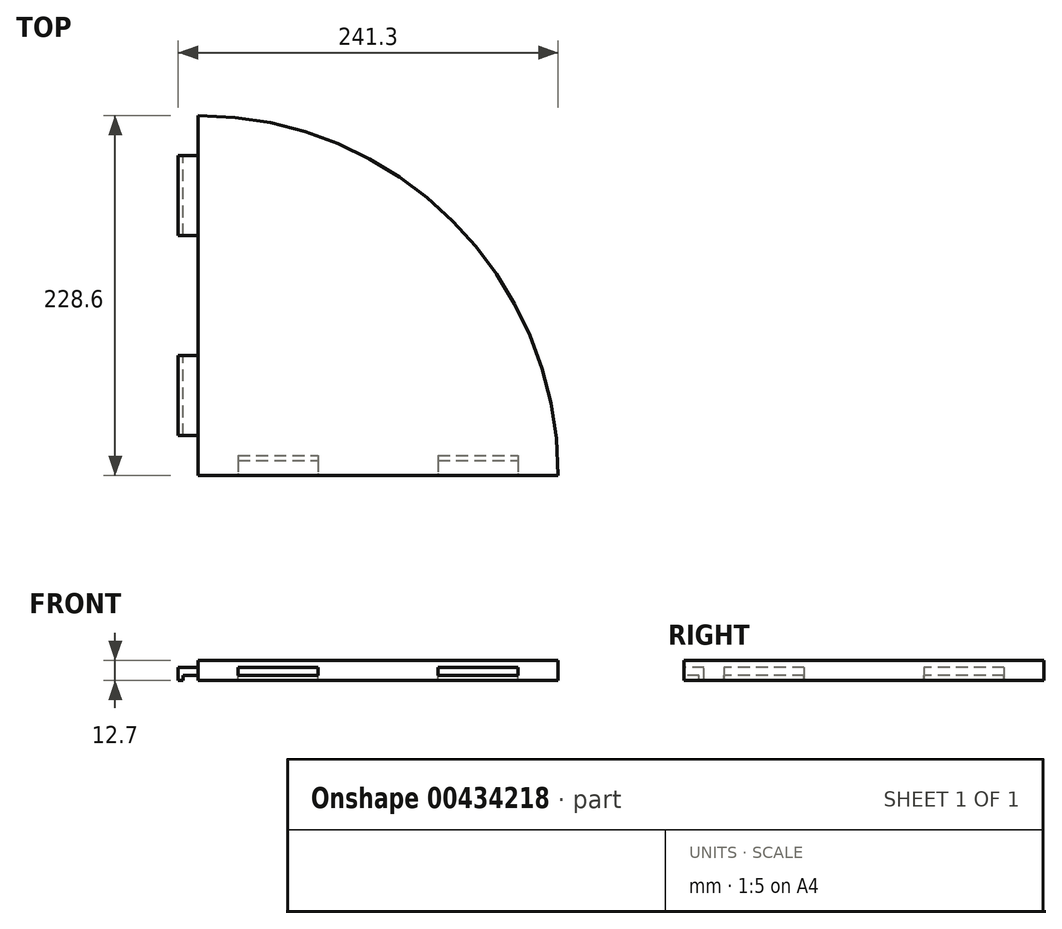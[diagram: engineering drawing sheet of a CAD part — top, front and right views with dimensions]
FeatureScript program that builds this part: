
annotation { "Feature Type Name" : "Feature", "Feature Type Description" : "" }
export const myFeature = defineFeature(function(context is Context, id is Id, definition is map)
    precondition{}
    {
        {
            var Q0;
            Q0=qCreatedBy(makeId("Top.planeOp"),FACE);
            var sketch = newSketch(context, id + "F0", { "sketchPlane" : qUnion([Q0])});
            skLineSegment(sketch, "E0", {"start": v(0, 0) * mm, "end": v(0, 228.6) * mm});
            skLineSegment(sketch, "E1", {"start": v(0, 0) * mm, "end": v(228.6, 0) * mm});
            skArc(sketch, "E2", {"start": v(0, 228.6) * mm, "mid": v(161.64, 161.64) * mm, "end": v(228.6, 0) * mm});
            skSolve(sketch);
        }
        {
            var Q0;
            Q0 = qSketchRegion(id + "F0", true);
            extrude(context, id + "F1", {"entities" : qUnion([Q0]), "depth" : 12.7 * mm});
        }
        {
            var Q0;
            Q0=makeQuery(id+"F1.opExtrude","SWEPT_FACE",FACE,{"disambiguationData":[OSD([sQuery(id+"F0.wireOp",EDGE,"E1")])]});
            var sketch = newSketch(context, id + "F2", { "sketchPlane" : qUnion([Q0])});
            skLineSegment(sketch, "E3.bottom", {"start": v(25.4, 3.18) * mm, "end": v(76.2, 3.18) * mm});
            skLineSegment(sketch, "E3.top", {"start": v(25.4, 8.26) * mm, "end": v(76.2, 8.26) * mm});
            skLineSegment(sketch, "E3.left", {"start": v(25.4, 3.18) * mm, "end": v(25.4, 8.26) * mm});
            skLineSegment(sketch, "E3.right", {"start": v(76.2, 3.18) * mm, "end": v(76.2, 8.25) * mm});
            skLineSegment(sketch, "E4.bottom", {"start": v(152.4, 3.18) * mm, "end": v(203.2, 3.18) * mm});
            skLineSegment(sketch, "E4.top", {"start": v(152.4, 8.25) * mm, "end": v(203.2, 8.25) * mm});
            skLineSegment(sketch, "E4.left", {"start": v(152.4, 3.18) * mm, "end": v(152.4, 8.25) * mm});
            skLineSegment(sketch, "E4.right", {"start": v(203.2, 3.18) * mm, "end": v(203.2, 8.26) * mm});
            skSolve(sketch);
        }
        {
            var Q0;
            Q0 = qSketchRegion(id + "F2", true);
            extrude(context, id + "F3", {"entities" : qUnion([Q0]), "operationType" : NewBodyOperationType.REMOVE, "oppositeDirection" : true, "depth" : 12.7 * mm, "offsetDistance" : 25.4 * mm});
        }
        {
            var Q0;
            Q0=makeQuery(id+"F1.opExtrude","SWEPT_FACE",FACE,{"disambiguationData":[OSD([sQuery(id+"F0.wireOp",EDGE,"E0")])]});
            var sketch = newSketch(context, id + "F4", { "sketchPlane" : qUnion([Q0])});
            skLineSegment(sketch, "E5.bottom", {"start": v(-76.2, 8.26) * mm, "end": v(-25.4, 8.26) * mm});
            skLineSegment(sketch, "E5.top", {"start": v(-76.2, 3.17) * mm, "end": v(-25.4, 3.17) * mm});
            skLineSegment(sketch, "E5.left", {"start": v(-76.2, 8.26) * mm, "end": v(-76.2, 3.17) * mm});
            skLineSegment(sketch, "E5.right", {"start": v(-25.4, 8.26) * mm, "end": v(-25.4, 3.18) * mm});
            skLineSegment(sketch, "E6.bottom", {"start": v(-203.2, 8.26) * mm, "end": v(-152.4, 8.26) * mm});
            skLineSegment(sketch, "E6.top", {"start": v(-203.2, 3.17) * mm, "end": v(-152.4, 3.17) * mm});
            skLineSegment(sketch, "E6.left", {"start": v(-203.2, 8.26) * mm, "end": v(-203.2, 3.18) * mm});
            skLineSegment(sketch, "E6.right", {"start": v(-152.4, 8.26) * mm, "end": v(-152.4, 3.18) * mm});
            skSolve(sketch);
        }
        {
            var Q0;
            Q0 = qSketchRegion(id + "F4", true);
            extrude(context, id + "F5", {"entities" : qUnion([Q0]), "operationType" : NewBodyOperationType.ADD, "depth" : 12.7 * mm, "offsetDistance" : 25.4 * mm});
        }
        {
            var Q0;
            Q0=makeQuery(id+"F3.boolean.opBoolean","COPY",FACE,{"derivedFrom":makeQuery(id+"F3.opExtrude","SWEPT_FACE",FACE,{"disambiguationData":[OSD([sQuery(id+"F2.wireOp",EDGE,"E3.bottom")])]})});
            var sketch = newSketch(context, id + "F6", { "sketchPlane" : qUnion([Q0])});
            skLineSegment(sketch, "E7.bottom", {"start": v(25.4, 12.7) * mm, "end": v(76.2, 12.7) * mm});
            skLineSegment(sketch, "E7.top", {"start": v(25.4, 9.52) * mm, "end": v(76.2, 9.52) * mm});
            skLineSegment(sketch, "E7.left", {"start": v(25.4, 12.7) * mm, "end": v(25.4, 9.52) * mm});
            skLineSegment(sketch, "E7.right", {"start": v(76.2, 12.7) * mm, "end": v(76.2, 9.52) * mm});
            skLineSegment(sketch, "E8.bottom", {"start": v(152.4, 12.7) * mm, "end": v(203.2, 12.7) * mm});
            skLineSegment(sketch, "E8.top", {"start": v(152.4, 9.52) * mm, "end": v(203.2, 9.52) * mm});
            skLineSegment(sketch, "E8.left", {"start": v(152.4, 12.7) * mm, "end": v(152.4, 9.52) * mm});
            skLineSegment(sketch, "E8.right", {"start": v(203.2, 12.7) * mm, "end": v(203.2, 9.52) * mm});
            skSolve(sketch);
        }
        {
            var Q0;
            Q0 = qSketchRegion(id + "F6", true);
            extrude(context, id + "F7", {"entities" : qUnion([Q0]), "operationType" : NewBodyOperationType.REMOVE, "endBound" : BoundingType.THROUGH_ALL, "oppositeDirection" : true, "depth" : 25.4 * mm, "offsetDistance" : 25.4 * mm});
        }
        {
            var Q0;
            Q0=makeQuery(id+"F5.opExtrude","SWEPT_FACE",FACE,{"disambiguationData":[OSD([sQuery(id+"F4.wireOp",EDGE,"E6.top")])]});
            var sketch = newSketch(context, id + "F8", { "sketchPlane" : qUnion([Q0])});
            skLineSegment(sketch, "E9.bottom", {"start": v(-12.7, -152.4) * mm, "end": v(-9.52, -152.4) * mm});
            skLineSegment(sketch, "E9.top", {"start": v(-12.7, -203.2) * mm, "end": v(-9.52, -203.2) * mm});
            skLineSegment(sketch, "E9.left", {"start": v(-12.7, -152.4) * mm, "end": v(-12.7, -203.2) * mm});
            skLineSegment(sketch, "E9.right", {"start": v(-9.53, -152.4) * mm, "end": v(-9.52, -203.2) * mm});
            skLineSegment(sketch, "E10.bottom", {"start": v(-12.7, -25.4) * mm, "end": v(-9.53, -25.4) * mm});
            skLineSegment(sketch, "E10.top", {"start": v(-12.7, -76.2) * mm, "end": v(-9.52, -76.2) * mm});
            skLineSegment(sketch, "E10.left", {"start": v(-12.7, -25.4) * mm, "end": v(-12.7, -76.2) * mm});
            skLineSegment(sketch, "E10.right", {"start": v(-9.53, -25.4) * mm, "end": v(-9.52, -76.2) * mm});
            skSolve(sketch);
        }
        {
            var Q0;
            Q0 = qSketchRegion(id + "F8", true);
            extrude(context, id + "F9", {"entities" : qUnion([Q0]), "operationType" : NewBodyOperationType.ADD, "depth" : 3.17 * mm, "offsetDistance" : 25.4 * mm});
        }
    });
